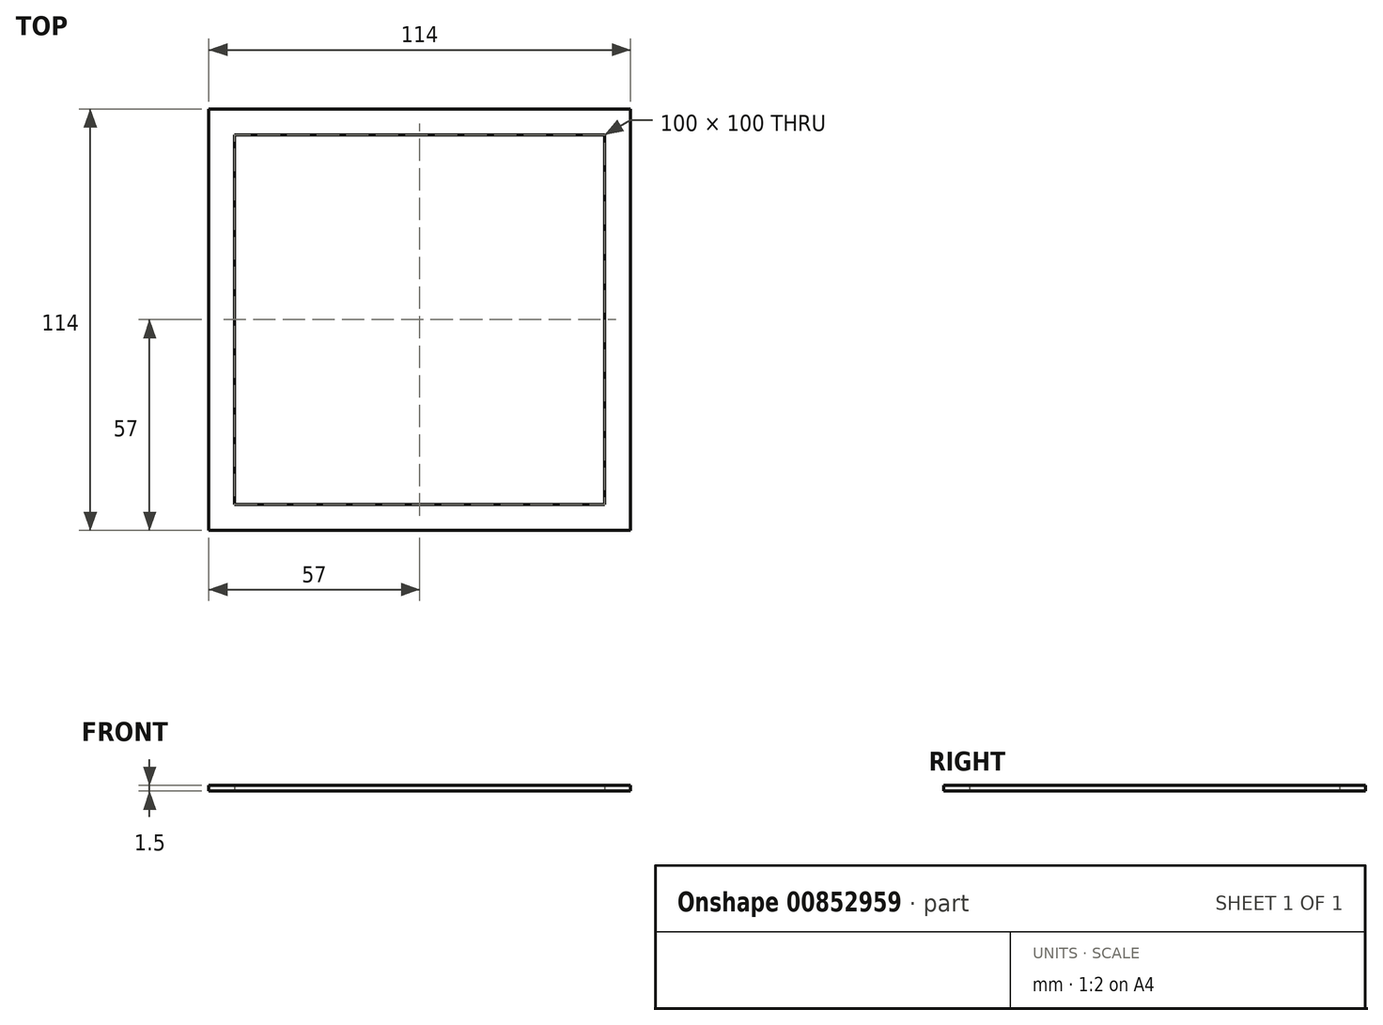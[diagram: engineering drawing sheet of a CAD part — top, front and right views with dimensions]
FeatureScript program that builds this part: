
annotation { "Feature Type Name" : "Feature", "Feature Type Description" : "" }
export const myFeature = defineFeature(function(context is Context, id is Id, definition is map)
    precondition{}
    {
        {
            var Q0;
            Q0=qCreatedBy(makeId("Top.planeOp"),FACE);
            var sketch = newSketch(context, id + "F0", { "sketchPlane" : qUnion([Q0])});
            skLineSegment(sketch, "E0.bottom", {"start": v(-57, 57) * mm, "end": v(57, 57) * mm});
            skLineSegment(sketch, "E0.top", {"start": v(-57, -57) * mm, "end": v(57, -57) * mm});
            skLineSegment(sketch, "E0.left", {"start": v(-57, 57) * mm, "end": v(-57, -57) * mm});
            skLineSegment(sketch, "E0.right", {"start": v(57, 57) * mm, "end": v(57, -57) * mm});
            skPoint(sketch, "E0.middle", {"position": v(0, 0) * mm});
            skSolve(sketch);
        }
        {
            var Q0;
            Q0=qSketchRegion(id+"F0",true);
            extrude(context, id + "F1", {"entities" : qUnion([Q0]), "depth" : 1.5 * mm, "offsetDistance" : 25 * mm});
        }
        {
            var Q0;
            Q0=qCreatedBy(makeId("Top.planeOp"),FACE);
            var sketch = newSketch(context, id + "F2", { "sketchPlane" : qUnion([Q0])});
            skLineSegment(sketch, "E1.bottom", {"start": v(-50, 50) * mm, "end": v(50, 50) * mm});
            skLineSegment(sketch, "E1.top", {"start": v(-50, -50) * mm, "end": v(50, -50) * mm});
            skLineSegment(sketch, "E1.left", {"start": v(-50, 50) * mm, "end": v(-50, -50) * mm});
            skLineSegment(sketch, "E1.right", {"start": v(50, 50) * mm, "end": v(50, -50) * mm});
            skPoint(sketch, "E1.middle", {"position": v(0, 0) * mm});
            skSolve(sketch);
        }
        {
            var Q0;
            Q0=qSketchRegion(id+"F2",true);
            extrude(context, id + "F3", {"entities" : qUnion([Q0]), "operationType" : NewBodyOperationType.REMOVE, "endBound" : BoundingType.THROUGH_ALL, "depth" : 25 * mm, "offsetDistance" : 25 * mm});
        }
    });
